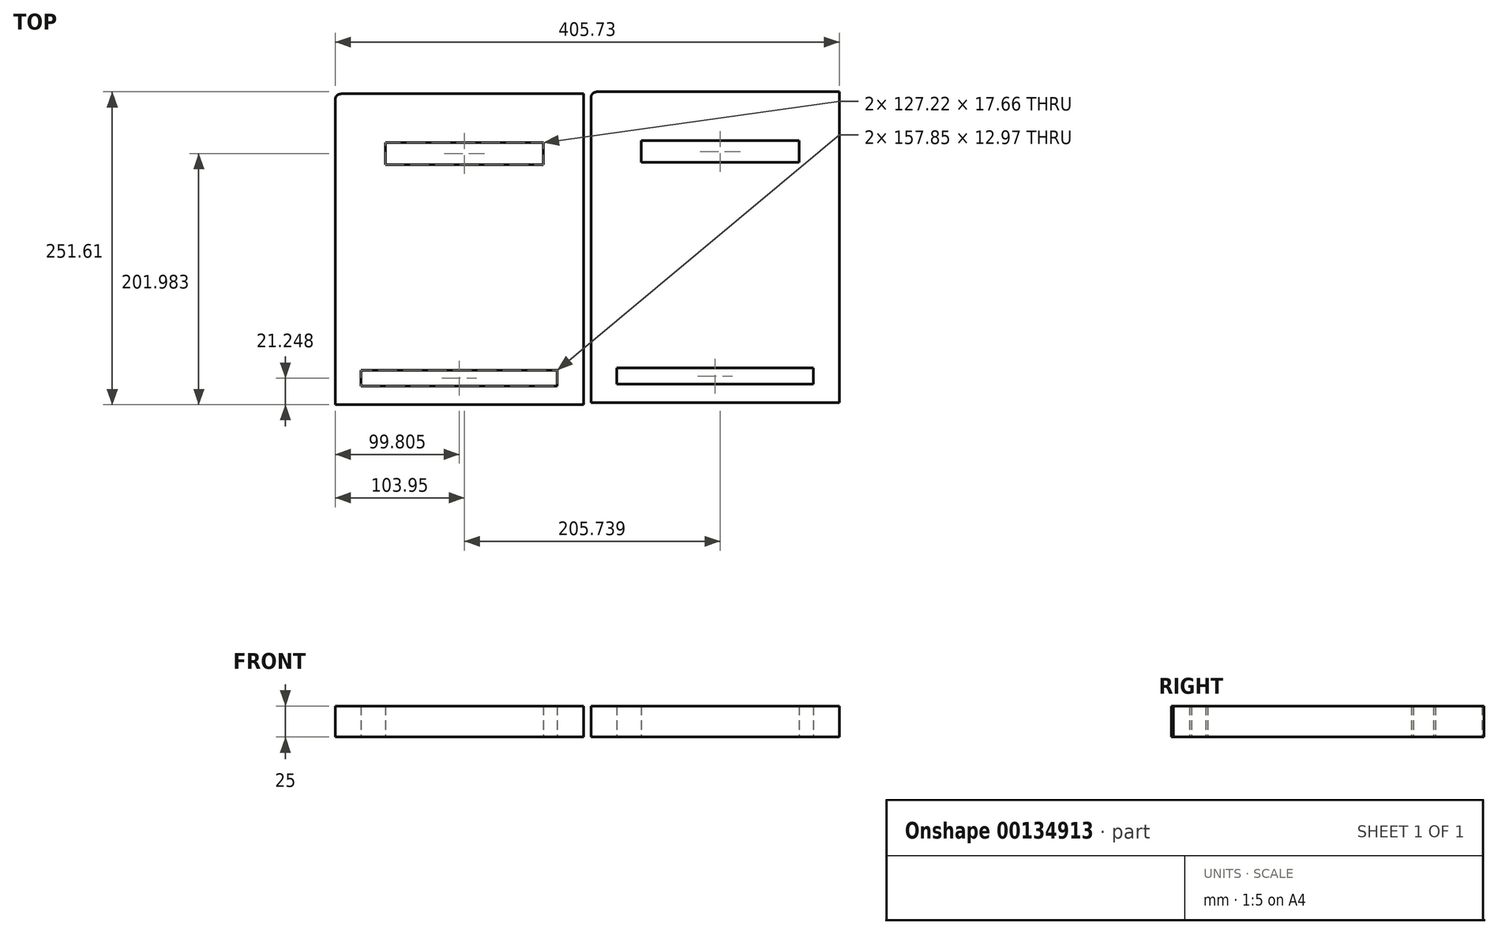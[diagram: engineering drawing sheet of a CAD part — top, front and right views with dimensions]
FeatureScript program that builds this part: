
annotation { "Feature Type Name" : "Feature", "Feature Type Description" : "" }
export const myFeature = defineFeature(function(context is Context, id is Id, definition is map)
    precondition{}
    {
        {
            var Q0;
            Q0=qCreatedBy(makeId("Top.planeOp"),FACE);
            var sketch = newSketch(context, id + "F0", { "sketchPlane" : qUnion([Q0])});
            skLineSegment(sketch, "E0.bottom", {"start": v(-104.35, 151.77) * mm, "end": v(90.65, 151.77) * mm});
            skLineSegment(sketch, "E0.top", {"start": v(-109.35, -98.23) * mm, "end": v(90.65, -98.23) * mm});
            skLineSegment(sketch, "E0.left", {"start": v(-109.35, 146.77) * mm, "end": v(-109.35, -98.23) * mm});
            skLineSegment(sketch, "E0.right", {"start": v(90.65, 151.77) * mm, "end": v(90.65, -98.23) * mm});
            skLineSegment(sketch, "E1.bottom", {"start": v(-69, 112.58) * mm, "end": v(58.2, 112.58) * mm});
            skLineSegment(sketch, "E1.top", {"start": v(-69, 94.92) * mm, "end": v(58.2, 94.92) * mm});
            skLineSegment(sketch, "E1.left", {"start": v(-69, 112.58) * mm, "end": v(-69, 94.92) * mm});
            skLineSegment(sketch, "E1.right", {"start": v(58.2, 112.58) * mm, "end": v(58.2, 94.92) * mm});
            skLineSegment(sketch, "E2.bottom", {"start": v(69.38, -83.47) * mm, "end": v(-88.47, -83.47) * mm});
            skLineSegment(sketch, "E2.top", {"start": v(69.38, -70.5) * mm, "end": v(-88.47, -70.5) * mm});
            skLineSegment(sketch, "E2.left", {"start": v(69.38, -83.47) * mm, "end": v(69.38, -70.5) * mm});
            skLineSegment(sketch, "E2.right", {"start": v(-88.47, -83.47) * mm, "end": v(-88.47, -70.5) * mm});
            skPoint(sketch, "E3.visualSharp", {"position": v(-109.35, 151.77) * mm});
            skArc(sketch, "E3.filletArc", {"start": v(-104.35, 151.77) * mm, "mid": v(-107.9, 150.3) * mm, "end": v(-109.35, 146.77) * mm});
            skLineSegment(sketch, "E4.bottom", {"start": v(101.38, 153.38) * mm, "end": v(296.38, 153.38) * mm});
            skLineSegment(sketch, "E4.top", {"start": v(96.38, -96.62) * mm, "end": v(296.38, -96.62) * mm});
            skLineSegment(sketch, "E4.left", {"start": v(96.38, 148.38) * mm, "end": v(96.38, -96.62) * mm});
            skLineSegment(sketch, "E4.right", {"start": v(296.38, 153.38) * mm, "end": v(296.38, -96.62) * mm});
            skLineSegment(sketch, "E5.bottom", {"start": v(136.73, 114.2) * mm, "end": v(263.95, 114.2) * mm});
            skLineSegment(sketch, "E5.top", {"start": v(136.73, 96.54) * mm, "end": v(263.95, 96.54) * mm});
            skLineSegment(sketch, "E5.left", {"start": v(136.73, 114.2) * mm, "end": v(136.73, 96.54) * mm});
            skLineSegment(sketch, "E5.right", {"start": v(263.95, 114.2) * mm, "end": v(263.95, 96.54) * mm});
            skLineSegment(sketch, "E6.bottom", {"start": v(275.12, -81.86) * mm, "end": v(117.27, -81.86) * mm});
            skLineSegment(sketch, "E6.top", {"start": v(275.12, -68.88) * mm, "end": v(117.27, -68.88) * mm});
            skLineSegment(sketch, "E6.left", {"start": v(275.12, -81.86) * mm, "end": v(275.12, -68.88) * mm});
            skLineSegment(sketch, "E6.right", {"start": v(117.27, -81.86) * mm, "end": v(117.27, -68.88) * mm});
            skPoint(sketch, "E7.visualSharp", {"position": v(96.38, 153.38) * mm});
            skArc(sketch, "E7.filletArc", {"start": v(101.38, 153.38) * mm, "mid": v(97.85, 151.91) * mm, "end": v(96.38, 148.38) * mm});
            skSolve(sketch);
        }
        {
            var Q0;
            Q0=makeQuery(id+"F0.imprint","IMPRINT",FACE,{"disambiguationData":[TD([[makeQuery(id+"F0.imprint","IMPRINT",EDGE,{"derivedFrom":sQuery(id+"F0.wireOp",EDGE,"E4.bottom")}),-1.0]])]});
            var Q1;
            Q1=makeQuery(id+"F0.imprint","IMPRINT",FACE,{"disambiguationData":[TD([[makeQuery(id+"F0.imprint","IMPRINT",EDGE,{"derivedFrom":sQuery(id+"F0.wireOp",EDGE,"E0.bottom")}),-1.0]])]});
            extrude(context, id + "F1", {"entities" : qUnion([Q0, Q1]), "depth" : 25 * mm});
        }
    });
